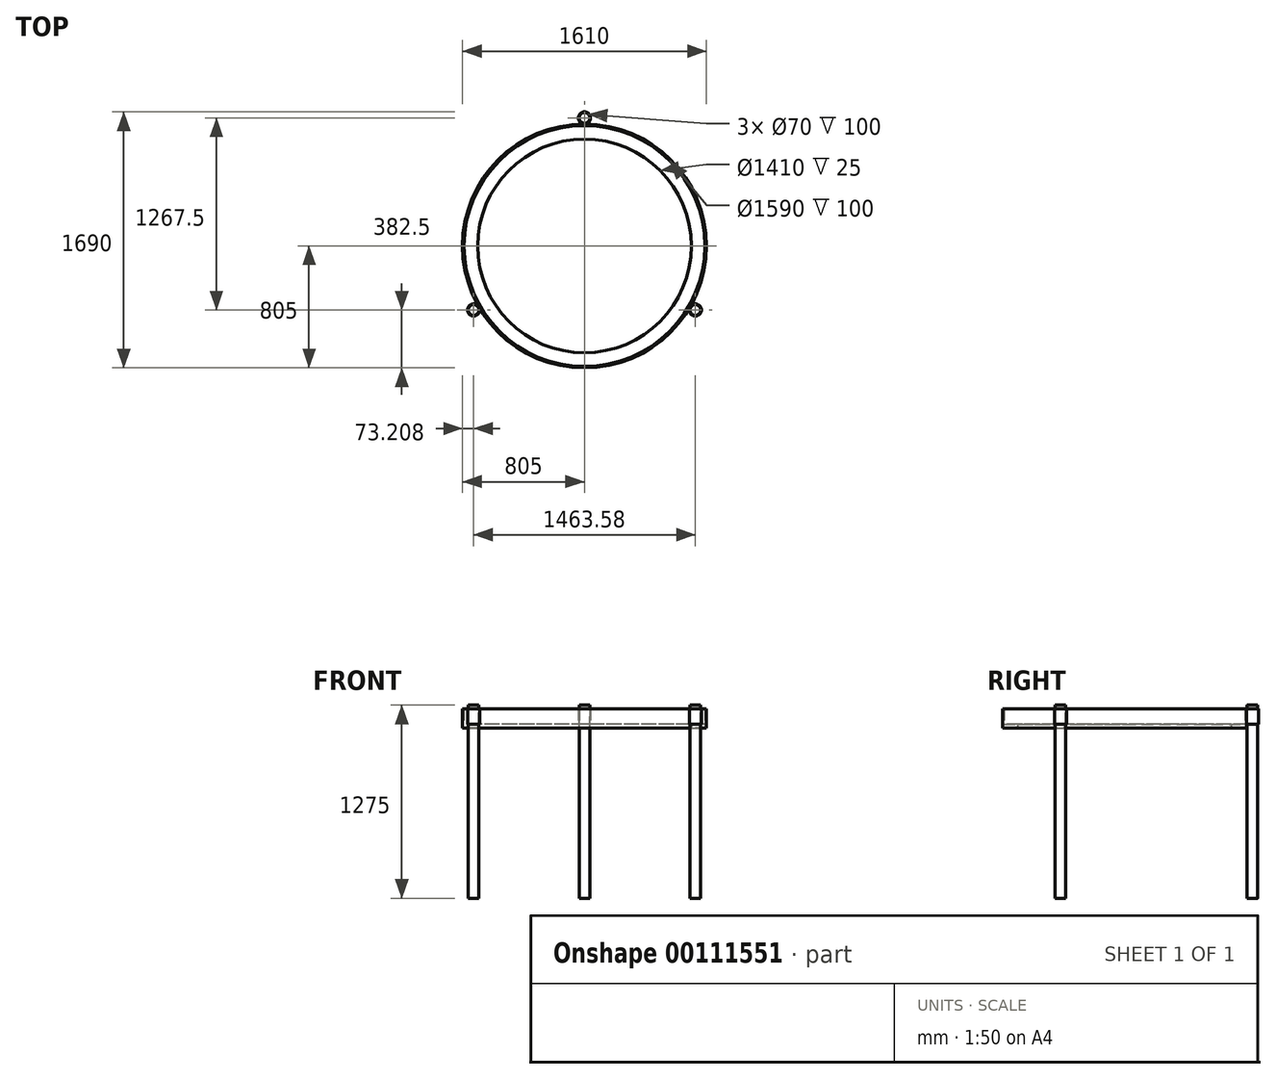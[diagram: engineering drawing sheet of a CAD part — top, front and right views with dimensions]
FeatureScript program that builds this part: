
annotation { "Feature Type Name" : "Feature", "Feature Type Description" : "" }
export const myFeature = defineFeature(function(context is Context, id is Id, definition is map)
    precondition{}
    {
        {
            var Q0;
            Q0=qCreatedBy(makeId("Top.planeOp"),FACE);
            var sketch = newSketch(context, id + "F0", { "sketchPlane" : qUnion([Q0])});
            skCircle(sketch, "E0", {"center": v(0, 0) * mm, "radius": 805 * mm});
            skCircle(sketch, "E1", {"center": v(0, 0) * mm, "radius": 705 * mm});
            skSolve(sketch);
        }
        {
            var Q0;
            Q0 = qSketchRegion(id + "F0", true);
            extrude(context, id + "F1", {"entities" : qUnion([Q0]), "depth" : 25 * mm});
        }
        {
            var Q0;
            Q0=makeQuery(id+"F1.opExtrude","CAP_FACE",FACE,{"disambiguationData":[OSD([sQuery(id+"F0.wireOp",EDGE,"E0"),sQuery(id+"F0.wireOp",EDGE,"E1")])],"isStart":false});
            var sketch = newSketch(context, id + "F2", { "sketchPlane" : qUnion([Q0])});
            skCircle(sketch, "E2", {"center": v(0, 0) * mm, "radius": 805 * mm});
            skCircle(sketch, "E3", {"center": v(0, 0) * mm, "radius": 795 * mm});
            skCircle(sketch, "E4", {"center": v(0, 845) * mm, "radius": 40 * mm});
            skCircle(sketch, "E5", {"center": v(0, 845) * mm, "radius": 35 * mm});
            skCircle(sketch, "E6.1.0", {"center": v(-731.8, -422.5) * mm, "radius": 35 * mm});
            skCircle(sketch, "E6.1.1", {"center": v(-731.8, -422.5) * mm, "radius": 40 * mm});
            skCircle(sketch, "E6.2.0", {"center": v(731.8, -422.5) * mm, "radius": 35 * mm});
            skCircle(sketch, "E6.2.1", {"center": v(731.8, -422.5) * mm, "radius": 40 * mm});
            skSolve(sketch);
        }
        {
            var Q0;
            Q0 = qSketchRegion(id + "F2", true);
            extrude(context, id + "F3", {"entities" : qUnion([Q0]), "operationType" : NewBodyOperationType.ADD, "depth" : 100 * mm});
        }
        {
            var Q0;
            Q0=makeQuery(id+"F3.opExtrude","CAP_FACE",FACE,{"disambiguationData":[OSD([sQuery(id+"F2.wireOp",EDGE,"E4"),sQuery(id+"F2.wireOp",EDGE,"E5")])],"isStart":false});
            var sketch = newSketch(context, id + "F4", { "sketchPlane" : qUnion([Q0])});
            skCircle(sketch, "E7", {"center": v(0, 845) * mm, "radius": 35 * mm});
            skPoint(sketch, "E7.first.point", {"position": v(22.32, 871.96) * mm});
            skPoint(sketch, "E7.second.point", {"position": v(-22.32, 818.04) * mm});
            skPoint(sketch, "E7.third.point", {"position": v(27.76, 823.68) * mm});
            skPoint(sketch, "E8.1.0", {"position": v(-766.3, -416.65) * mm});
            skPoint(sketch, "E8.1.1", {"position": v(-697.28, -428.35) * mm});
            skPoint(sketch, "E8.1.2", {"position": v(-727.2, -387.8) * mm});
            skCircle(sketch, "E8.1.3", {"center": v(-731.8, -422.5) * mm, "radius": 35 * mm});
            skPoint(sketch, "E8.2.0", {"position": v(743.98, -455.3) * mm});
            skPoint(sketch, "E8.2.1", {"position": v(719.6, -389.7) * mm});
            skPoint(sketch, "E8.2.2", {"position": v(699.45, -435.88) * mm});
            skCircle(sketch, "E8.2.3", {"center": v(731.8, -422.5) * mm, "radius": 35 * mm});
            skPoint(sketch, "E8.center", {"position": v(0, 0) * mm});
            skSolve(sketch);
        }
        {
            var Q0;
            Q0 = qSketchRegion(id + "F4", true);
            extrude(context, id + "F5", {"entities" : qUnion([Q0]), "oppositeDirection" : true, "depth" : (1150 + 100) * mm, "hasSecondDirection" : true, "secondDirectionOppositeDirection" : false, "secondDirectionDepth" : 25 * mm});
        }
    });
